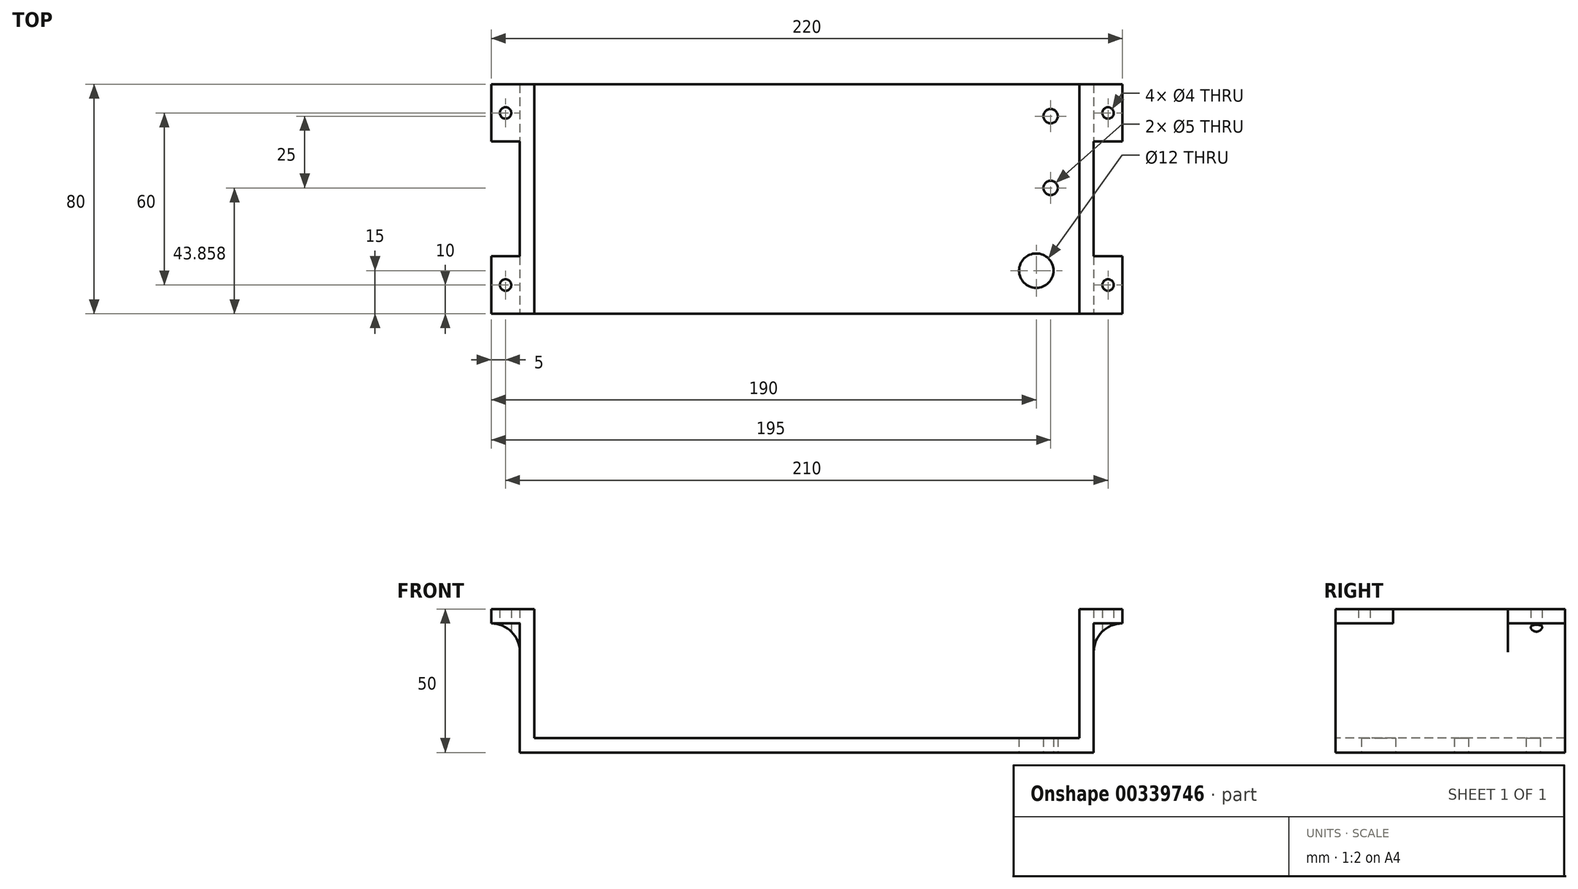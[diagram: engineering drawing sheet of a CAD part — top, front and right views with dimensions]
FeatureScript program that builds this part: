
annotation { "Feature Type Name" : "Feature", "Feature Type Description" : "" }
export const myFeature = defineFeature(function(context is Context, id is Id, definition is map)
    precondition{}
    {
        {
            var Q0;
            Q0=qCreatedBy(makeId("Top.planeOp"),FACE);
            var sketch = newSketch(context, id + "F0", { "sketchPlane" : qUnion([Q0])});
            skLineSegment(sketch, "E0.bottom", {"start": v(0, 0) * mm, "end": v(200, 0) * mm});
            skLineSegment(sketch, "E0.top", {"start": v(0, -80) * mm, "end": v(200, -80) * mm});
            skLineSegment(sketch, "E0.left", {"start": v(0, 0) * mm, "end": v(0, -80) * mm});
            skLineSegment(sketch, "E0.right", {"start": v(200, 0) * mm, "end": v(200, -80) * mm});
            skLineSegment(sketch, "E1", {"start": v(200, -65) * mm, "end": v(180, -65) * mm});
            skLineSegment(sketch, "E2", {"start": v(180, -65) * mm, "end": v(180, -80) * mm});
            skCircle(sketch, "E3", {"center": v(180, -65) * mm, "radius": 6 * mm});
            skLineSegment(sketch, "E4", {"start": v(200, -36.14) * mm, "end": v(185, -36.14) * mm});
            skLineSegment(sketch, "E5", {"start": v(185, -36.14) * mm, "end": v(185, 0) * mm});
            skCircle(sketch, "E6", {"center": v(185, -36.14) * mm, "radius": 2.5 * mm});
            skCircle(sketch, "E7", {"center": v(185, -11.14) * mm, "radius": 2.5 * mm});
            skSolve(sketch);
        }
        {
            var Q0;
            Q0=makeQuery(id+"F0.imprint","IMPRINT",FACE,{"disambiguationData":[TD([[makeQuery(id+"F0.imprint","IMPRINT",EDGE,{"derivedFrom":sQuery(id+"F0.wireOp",EDGE,"E0.bottom")}),-1.0]])]});
            var Q1;
            {var subQ18=sQuery(id+"F0.wireOp",EDGE,"E0.left");Q1=makeQuery(id+"F0.imprint","IMPRINT",FACE,{"disambiguationData":[TD([[makeQuery(id+"F0.imprint","IMPRINT",EDGE,{"derivedFrom":subQ18}),1.0]])]});}
            var Q2;
            {var subQ1=sQuery(id+"F0.wireOp",EDGE,"E0.top");var subQ5=sQuery(id+"F0.wireOp",EDGE,"E0.right");var subQ6=makeQuery(id+"F0.imprint","INTERSECT",VERTEX,{"derivedFrom":[subQ1,subQ5]});Q2=makeQuery(id+"F0.imprint","IMPRINT",FACE,{"disambiguationData":[TD([[makeQuery(id+"F0.imprint","IMPRINT",EDGE,{"disambiguationData":[TD([[subQ6,1.0]])],"derivedFrom":subQ1}),1.0]])]});}
            extrude(context, id + "F1", {"entities" : qUnion([Q0, Q1, Q2]), "depth" : 5 * mm});
        }
        {
            var Q0;
            Q0=makeQuery(id+"F1.opExtrude","CAP_FACE",FACE,{"disambiguationData":[OSD([sQuery(id+"F0.wireOp",EDGE,"E0.bottom"),sQuery(id+"F0.wireOp",EDGE,"E0.top"),sQuery(id+"F0.wireOp",EDGE,"E0.left"),sQuery(id+"F0.wireOp",EDGE,"E0.right")])],"isStart":false});
            var sketch = newSketch(context, id + "F2", { "sketchPlane" : qUnion([Q0])});
            skLineSegment(sketch, "E8.bottom", {"start": v(0, 0) * mm, "end": v(5, 0) * mm});
            skLineSegment(sketch, "E8.top", {"start": v(0, -80) * mm, "end": v(5, -80) * mm});
            skLineSegment(sketch, "E8.left", {"start": v(0, 0) * mm, "end": v(0, -80) * mm});
            skLineSegment(sketch, "E8.right", {"start": v(5, 0) * mm, "end": v(5, -80) * mm});
            skLineSegment(sketch, "E9.bottom", {"start": v(200, 0) * mm, "end": v(195, 0) * mm});
            skLineSegment(sketch, "E9.top", {"start": v(200, -80) * mm, "end": v(195, -80) * mm});
            skLineSegment(sketch, "E9.left", {"start": v(200, 0) * mm, "end": v(200, -80) * mm});
            skLineSegment(sketch, "E9.right", {"start": v(195, 0) * mm, "end": v(195, -80) * mm});
            skSolve(sketch);
        }
        {
            var Q0;
            Q0=makeQuery(id+"F2.imprint","IMPRINT",FACE,{"disambiguationData":[TD([[makeQuery(id+"F2.imprint","IMPRINT",EDGE,{"derivedFrom":sQuery(id+"F2.wireOp",EDGE,"E8.bottom")}),-1.0]])]});
            var Q1;
            Q1=makeQuery(id+"F2.imprint","IMPRINT",FACE,{"disambiguationData":[TD([[makeQuery(id+"F2.imprint","IMPRINT",EDGE,{"derivedFrom":sQuery(id+"F2.wireOp",EDGE,"E9.bottom")}),-1.0]])]});
            extrude(context, id + "F3", {"entities" : qUnion([Q0, Q1]), "operationType" : NewBodyOperationType.ADD, "depth" : 40 * mm});
        }
        {
            var Q0;
            Q0=makeQuery(id+"F3.opExtrude","CAP_FACE",FACE,{"disambiguationData":[OSD([sQuery(id+"F2.wireOp",EDGE,"E8.bottom"),sQuery(id+"F2.wireOp",EDGE,"E8.top"),sQuery(id+"F2.wireOp",EDGE,"E8.left"),sQuery(id+"F2.wireOp",EDGE,"E8.right")])],"isStart":false});
            var sketch = newSketch(context, id + "F4", { "sketchPlane" : qUnion([Q0])});
            skPoint(sketch, "E10.oppositeSnap0", {"position": v(2.5, 0) * mm});
            skLineSegment(sketch, "E10.bottom", {"start": v(5, -80) * mm, "end": v(-10, -80) * mm});
            skLineSegment(sketch, "E10.top", {"start": v(5, 0) * mm, "end": v(-10, 0) * mm});
            skLineSegment(sketch, "E10.left", {"start": v(5, -80) * mm, "end": v(5, 0) * mm});
            skLineSegment(sketch, "E10.right", {"start": v(-10, -80) * mm, "end": v(-10, 0) * mm});
            skLineSegment(sketch, "E11.bottom", {"start": v(195, -80) * mm, "end": v(210, -80) * mm});
            skLineSegment(sketch, "E11.top", {"start": v(195, 0) * mm, "end": v(210, 0) * mm});
            skLineSegment(sketch, "E11.left", {"start": v(195, -80) * mm, "end": v(195, 0) * mm});
            skLineSegment(sketch, "E11.right", {"start": v(210, -80) * mm, "end": v(210, 0) * mm});
            skLineSegment(sketch, "E12", {"start": v(205, -80) * mm, "end": v(205, 0) * mm});
            skLineSegment(sketch, "E13", {"start": v(-5, -80) * mm, "end": v(-5, 0) * mm});
            skCircle(sketch, "E14", {"center": v(-5, -70) * mm, "radius": 2 * mm});
            skCircle(sketch, "E15", {"center": v(-5, -10) * mm, "radius": 2 * mm});
            skCircle(sketch, "E16", {"center": v(205, -10) * mm, "radius": 2 * mm});
            skCircle(sketch, "E17", {"center": v(205, -70) * mm, "radius": 2 * mm});
            skLineSegment(sketch, "E18", {"start": v(205, -70) * mm, "end": v(205, -40) * mm});
            skLineSegment(sketch, "E19", {"start": v(205, -40) * mm, "end": v(205, -10) * mm});
            skLineSegment(sketch, "E20", {"start": v(-5, -70) * mm, "end": v(-5, -40) * mm});
            skLineSegment(sketch, "E21", {"start": v(-5, -40) * mm, "end": v(-5, -10) * mm});
            skLineSegment(sketch, "E22", {"start": v(-10, -20) * mm, "end": v(0, -20) * mm});
            skLineSegment(sketch, "E23", {"start": v(-10, -60) * mm, "end": v(0, -60) * mm});
            skLineSegment(sketch, "E24", {"start": v(195, -60) * mm, "end": v(210, -60) * mm});
            skLineSegment(sketch, "E25", {"start": v(210, -20) * mm, "end": v(195, -20) * mm});
            skLineSegment(sketch, "E26", {"start": v(200, -20) * mm, "end": v(200, -60) * mm});
            skSolve(sketch);
        }
        {
            var Q0;
            {var subQ2=sQuery(id+"F4.wireOp",EDGE,"E10.left");Q0=makeQuery(id+"F4.imprint","IMPRINT",FACE,{"disambiguationData":[TD([[makeQuery(id+"F4.imprint","IMPRINT",EDGE,{"derivedFrom":subQ2}),-1.0]])]});}
            var Q1;
            {var subQ5=sQuery(id+"F4.wireOp",EDGE,"E11.left");var subQ6=sQuery(id+"F4.wireOp",EDGE,"E11.bottom");var subQ7=makeQuery(id+"F4.imprint","INTERSECT",VERTEX,{"derivedFrom":[subQ6,subQ5]});Q1=makeQuery(id+"F4.imprint","IMPRINT",FACE,{"disambiguationData":[TD([[makeQuery(id+"F4.imprint","IMPRINT",EDGE,{"disambiguationData":[TD([[subQ7,-1.0]])],"derivedFrom":subQ6}),1.0]])]});}
            var Q2;
            {var subQ5=sQuery(id+"F4.wireOp",EDGE,"E11.bottom");var subQ8=sQuery(id+"F4.wireOp",EDGE,"E11.right");var subQ11=makeQuery(id+"F4.imprint","INTERSECT",VERTEX,{"derivedFrom":[subQ5,subQ8]});Q2=makeQuery(id+"F4.imprint","IMPRINT",FACE,{"disambiguationData":[TD([[makeQuery(id+"F4.imprint","IMPRINT",EDGE,{"disambiguationData":[TD([[subQ11,1.0]])],"derivedFrom":subQ5}),1.0]])]});}
            var Q3;
            {var subQ1=sQuery(id+"F4.wireOp",EDGE,"E11.top");var subQ5=sQuery(id+"F4.wireOp",EDGE,"E11.left");var subQ6=makeQuery(id+"F4.imprint","INTERSECT",VERTEX,{"derivedFrom":[subQ1,subQ5]});Q3=makeQuery(id+"F4.imprint","IMPRINT",FACE,{"disambiguationData":[TD([[makeQuery(id+"F4.imprint","IMPRINT",EDGE,{"disambiguationData":[TD([[subQ6,-1.0]])],"derivedFrom":subQ1}),-1.0]])]});}
            var Q4;
            {var subQ0=sQuery(id+"F4.wireOp",EDGE,"E11.right");var subQ1=sQuery(id+"F4.wireOp",EDGE,"E11.top");var subQ2=makeQuery(id+"F4.imprint","INTERSECT",VERTEX,{"derivedFrom":[subQ1,subQ0]});Q4=makeQuery(id+"F4.imprint","IMPRINT",FACE,{"disambiguationData":[TD([[makeQuery(id+"F4.imprint","IMPRINT",EDGE,{"disambiguationData":[TD([[subQ2,1.0]])],"derivedFrom":subQ1}),-1.0]])]});}
            var Q5;
            {var subQ6=sQuery(id+"F4.wireOp",EDGE,"E10.right");var subQ9=sQuery(id+"F4.wireOp",EDGE,"E10.bottom");var subQ11=makeQuery(id+"F4.imprint","INTERSECT",VERTEX,{"derivedFrom":[subQ9,subQ6]});Q5=makeQuery(id+"F4.imprint","IMPRINT",FACE,{"disambiguationData":[TD([[makeQuery(id+"F4.imprint","IMPRINT",EDGE,{"disambiguationData":[TD([[subQ11,1.0]])],"derivedFrom":subQ9}),-1.0]])]});}
            var Q6;
            {var subQ5=sQuery(id+"F4.wireOp",EDGE,"E13");var subQ9=sQuery(id+"F4.wireOp",EDGE,"E10.bottom");var subQ10=makeQuery(id+"F4.imprint","INTERSECT",VERTEX,{"derivedFrom":[subQ9,subQ5]});Q6=makeQuery(id+"F4.imprint","IMPRINT",FACE,{"disambiguationData":[TD([[makeQuery(id+"F4.imprint","IMPRINT",EDGE,{"disambiguationData":[TD([[subQ10,1.0]])],"derivedFrom":subQ9}),-1.0]])]});}
            var Q7;
            {var subQ1=sQuery(id+"F4.wireOp",EDGE,"E10.top");var subQ5=sQuery(id+"F4.wireOp",EDGE,"E10.right");var subQ6=makeQuery(id+"F4.imprint","INTERSECT",VERTEX,{"derivedFrom":[subQ1,subQ5]});Q7=makeQuery(id+"F4.imprint","IMPRINT",FACE,{"disambiguationData":[TD([[makeQuery(id+"F4.imprint","IMPRINT",EDGE,{"disambiguationData":[TD([[subQ6,1.0]])],"derivedFrom":subQ1}),1.0]])]});}
            var Q8;
            {var subQ5=sQuery(id+"F4.wireOp",EDGE,"E13");var subQ7=sQuery(id+"F4.wireOp",EDGE,"E10.top");var subQ8=makeQuery(id+"F4.imprint","INTERSECT",VERTEX,{"derivedFrom":[subQ7,subQ5]});Q8=makeQuery(id+"F4.imprint","IMPRINT",FACE,{"disambiguationData":[TD([[makeQuery(id+"F4.imprint","IMPRINT",EDGE,{"disambiguationData":[TD([[subQ8,1.0]])],"derivedFrom":subQ7}),1.0]])]});}
            var Q9;
            {var subQ5=sQuery(id+"F4.wireOp",EDGE,"E26");Q9=makeQuery(id+"F4.imprint","IMPRINT",FACE,{"disambiguationData":[TD([[makeQuery(id+"F4.imprint","IMPRINT",EDGE,{"derivedFrom":subQ5}),-1.0]])]});}
            extrude(context, id + "F5", {"entities" : qUnion([Q0, Q1, Q2, Q3, Q4, Q5, Q6, Q7, Q8, Q9]), "operationType" : NewBodyOperationType.ADD, "depth" : 5 * mm});
        }
        {
            var Q0;
            {var subQ1=sQuery(id+"F2.wireOp",EDGE,"E9.left");Q0=makeQuery(id+"F5.boolean.opBoolean","SPLIT",EDGE,{"disambiguationData":[TD([makeQuery(id+"F1.opExtrude","SWEPT_FACE",FACE,{"disambiguationData":[OSD([sQuery(id+"F0.wireOp",EDGE,"E0.top")])]})])],"derivedFrom":makeQuery(id+"F3.opExtrude","CAP_EDGE",EDGE,{"disambiguationData":[OSD([subQ1])],"isStart":false})});}
            var Q1;
            {var subQ3=sQuery(id+"F2.wireOp",EDGE,"E9.left");Q1=makeQuery(id+"F5.boolean.opBoolean","SPLIT",EDGE,{"disambiguationData":[TD([makeQuery(id+"F1.opExtrude","SWEPT_FACE",FACE,{"disambiguationData":[OSD([sQuery(id+"F0.wireOp",EDGE,"E0.bottom")])]})])],"derivedFrom":makeQuery(id+"F3.opExtrude","CAP_EDGE",EDGE,{"disambiguationData":[OSD([subQ3])],"isStart":false})});}
            var Q2;
            {var subQ0=sQuery(id+"F2.wireOp",EDGE,"E8.left");Q2=makeQuery(id+"F5.boolean.opBoolean","SPLIT",EDGE,{"disambiguationData":[TD([makeQuery(id+"F1.opExtrude","SWEPT_FACE",FACE,{"disambiguationData":[OSD([sQuery(id+"F0.wireOp",EDGE,"E0.bottom")])]})])],"derivedFrom":makeQuery(id+"F3.opExtrude","CAP_EDGE",EDGE,{"disambiguationData":[OSD([subQ0])],"isStart":false})});}
            var Q3;
            {var subQ0=sQuery(id+"F2.wireOp",EDGE,"E8.left");Q3=makeQuery(id+"F5.boolean.opBoolean","SPLIT",EDGE,{"disambiguationData":[TD([makeQuery(id+"F1.opExtrude","SWEPT_FACE",FACE,{"disambiguationData":[OSD([sQuery(id+"F0.wireOp",EDGE,"E0.top")])]})])],"derivedFrom":makeQuery(id+"F3.opExtrude","CAP_EDGE",EDGE,{"disambiguationData":[OSD([subQ0])],"isStart":false})});}
            fillet(context, id + "F6", {"entities" : qUnion([Q0, Q1, Q2, Q3]), "radius" : 10 * mm, "tangentPropagation" : true, "allowEdgeOverflow" : false});
        }
    });
